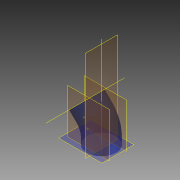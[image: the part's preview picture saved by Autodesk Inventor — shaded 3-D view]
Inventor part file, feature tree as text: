
AUTODESK INVENTOR PART (.ipt)
format: ipt  version: 2014 SP1 (Build 180222100, 222)  size: 165,888 bytes
history: native  units: in
note: dims shown in document units (in); Inventor stores cm internally (conversion verified against a paired STEP export)
features: plane x5, other x3, sketch x3, sweep x1, projected_geometry x1
ambient origin geometry x8: Origin, YZ Plane, XZ Plane, XY Plane, X Axis, Y Axis, Z Axis, Center Point
bodies: Solid1 (feature_tree)
feature tree (13):
  sweep  "Sweep1"
  plane  "Work Plane1"
  other  "Work Point1"
  other  "Work Point2"
  plane  "Work Plane4"
  plane  "Work Plane6"
  plane  "Work Plane7"
  plane  "Work Plane8"
  sketch  "Sketch4"  dims[d3=3.0in d4=8.0in d5=0.0in d6=0.05in d7=2.3in d8=-2.3in d14=0.7274in d15=0.7274in d16=0.7274in d17=3.0in d18=3.7274in d19=2.7574in d20=1.7574in d21=135.0deg]
  other  "Work Axis1"
  sketch  "Sketch1"  dims[d0=135.0deg d1=3.0in]
  sketch  "Sketch2"  dims[d2=4.0in]
  projected_geometry  "Project Cut Edges1"
